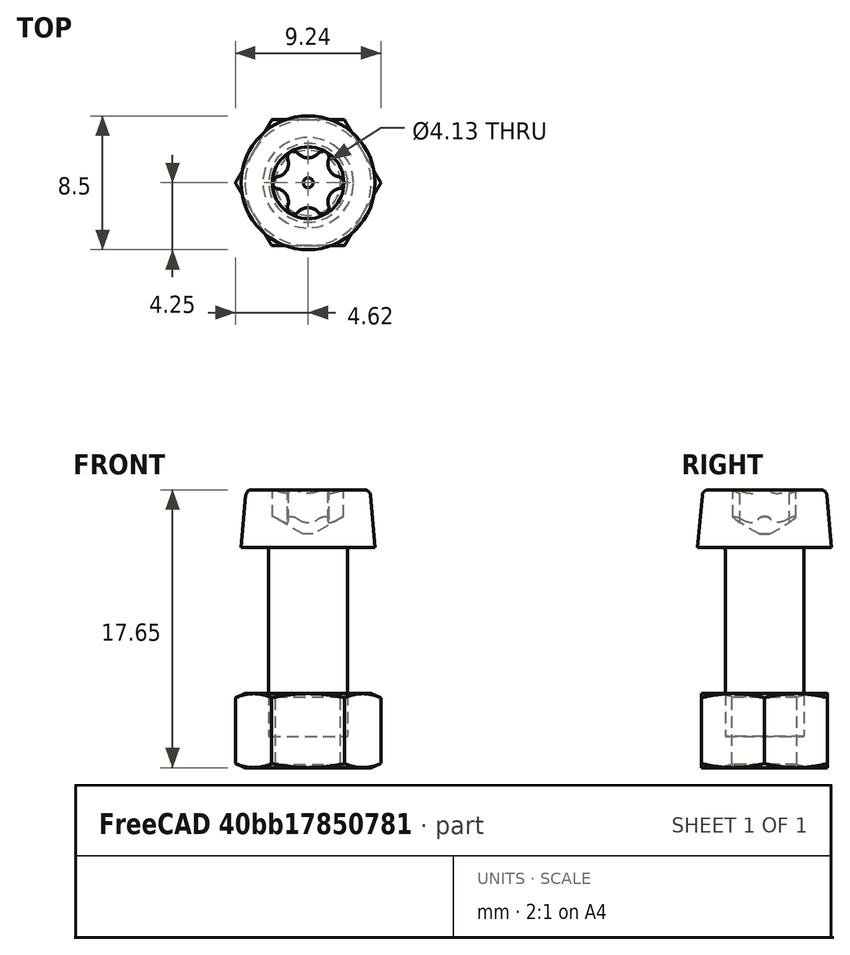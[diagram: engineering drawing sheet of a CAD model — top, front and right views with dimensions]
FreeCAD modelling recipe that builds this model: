
FCSTD DOCUMENT  (FreeCAD 0.20R29177 +426 (Git))
Label: assembly
License: All rights reserved
LicenseURL: http://en.wikipedia.org/wiki/All_rights_reserved
objects: App::DocumentObjectGroup×3, App::Link×3, Part::FeaturePython×2, PartDesign::CoordinateSystem×1, App::FeaturePython×1, App::Part×1
note: 3 computed .brp shape members not serialized (recipe doc carries the construction recipe); baked Part::Feature solids carry a one-line shape summary decoded from their .brp
EXTERNAL_REF file=clamp.FCStd obj=LCS_1
EXTERNAL_REF file=clamp.FCStd obj=Body
EXTERNAL_REF file=clamp.FCStd obj=CircleAxis_1
EXTERNAL_REF file=rectangle.FCStd obj=CircleAxis_1
EXTERNAL_REF file=rectangle.FCStd obj=Part

FEATURE [App::DocumentObjectGroup] Parts
FEATURE [PartDesign::CoordinateSystem] LCS_Origin
  AttacherType = Attacher::AttachEngine3D
  MapMode = 2
  Support = -> [X_Axis]
FEATURE [App::DocumentObjectGroup] Constraints
FEATURE [App::FeaturePython] Variables  # WARN: FeaturePython — macro-defined, semantics opaque (R4)
  Type = App::PropertyContainer
FEATURE [App::DocumentObjectGroup] Configurations
FEATURE [App::Link] clamp
  AttachedBy = #LCS_1
  AttachedTo = Parent Assembly#LCS_Origin
  LinkedObject = -> <external clamp.FCStd>#Body
  SolverId = Asm4EE
  expr: Placement = LCS_Origin.Placement * AttachmentOffset * clamp#LCS_1.Placement ^ -1
FEATURE [Part::FeaturePython] Screw  label="M5x12-Screw"  # WARN: FeaturePython — macro-defined, semantics opaque (R4)
  AttachedBy = Origin
  AttachedTo = clamp#CircleAxis_1
  Diameter = 7
  Invert = false
  LeftHanded = false
  Length = 3
  LengthCustom = 12
  MatchOuter = false
  OffsetAngle = 0
  Placement = pos=(-25,-5,3) rot=(0,0,1;3.14159rad)
  SolverId = Asm4EE
  Thread = false
  Type = 54
  expr: Placement = clamp.Placement * clamp#CircleAxis_1.Placement * AttachmentOffset
FEATURE [App::Link] RectanglePart
  AttachedBy = #CircleAxis_1
  AttachedTo = clamp#CircleAxis_1
  AttachmentOffset = pos=(0,0,-3) rot=(0,0,1;4.71239rad)
  LinkPlacement = pos=(-25,30,-3) rot=(0,0,-1;4.71239rad)
  LinkedObject = -> <external rectangle.FCStd>#Part
  Placement = pos=(-25,30,-3) rot=(0,0,-1;4.71239rad)
  SolverId = Asm4EE
  expr: Placement = clamp.Placement * clamp#CircleAxis_1.Placement * AttachmentOffset * rectangle#CircleAxis_1.Placement ^ -1
FEATURE [Part::FeaturePython] Nut  label="M5-Nut"  # WARN: FeaturePython — macro-defined, semantics opaque (R4)
  AttachedBy = Origin
  AttachedTo = clamp#CircleAxis_1
  AttachmentOffset = pos=(0,0,-14) rot=(0,0,1;0rad)
  Diameter = 7
  Invert = false
  LeftHanded = false
  MatchOuter = false
  OffsetAngle = 0
  Placement = pos=(-25,-5,-11) rot=(0,0,1;3.14159rad)
  SolverId = Asm4EE
  Thread = false
  Type = 31
  expr: Placement = clamp.Placement * clamp#CircleAxis_1.Placement * AttachmentOffset
FEATURE [App::Link] Body
  AttachedBy = #CircleAxis_1
  AttachedTo = clamp#CircleAxis_1
  AttachmentOffset = pos=(0,0,-9) rot=(1,0,0;3.14159rad)
  LinkPlacement = pos=(0,-10,-3) rot=(-1,0,0;3.14159rad)
  LinkedObject = -> <external clamp.FCStd>#Body
  Placement = pos=(0,-10,-3) rot=(-1,0,0;3.14159rad)
  SolverId = Asm4EE
  expr: Placement = clamp.Placement * clamp#CircleAxis_1.Placement * AttachmentOffset * clamp#CircleAxis_1.Placement ^ -1
FEATURE [App::Part] Assembly
  AssemblyType = Part::Link
  Group = -> [LCS_Origin,Constraints,Variables,Configurations,clamp,Screw,RectanglePart,Nut,Body]
  Origin = -> Origin
  Type = Assembly

RESOLVED EXTERNAL PARTS (link-assembly join: the EXTERNAL_REF files above that resolve inside this repo's crawl, each included once):
---- part clamp.FCStd = doc fcstd_29977836d994 ----
FCSTD DOCUMENT  (FreeCAD 0.20R29177 +426 (Git))
Label: clamp
License: All rights reserved
LicenseURL: http://en.wikipedia.org/wiki/All_rights_reserved
objects: Sketcher::SketchObject×2, PartDesign::Pad×1, PartDesign::Pocket×1, PartDesign::CoordinateSystem×1, PartDesign::Line×1, PartDesign::Body×1
note: 9 computed .brp shape members not serialized (recipe doc carries the construction recipe); baked Part::Feature solids carry a one-line shape summary decoded from their .brp

FEATURE [Sketcher::SketchObject] Sketch
  FullyConstrained = true
  MapMode = 5
  Placement = pos=(0,0,0) rot=(1,0,0;1.5708rad)
  Support = -> [XZ_Plane]
  sketch-geometry (10):
    g0: LineSegment StartX=-30 StartY=0 StartZ=0 EndX=-17 EndY=0 EndZ=0
    g1: LineSegment StartX=-30 StartY=0 StartZ=0 EndX=-30 EndY=3 EndZ=0
    g2: LineSegment StartX=30 StartY=3 StartZ=0 EndX=30 EndY=0 EndZ=0
    g3: ArcOfCircle CenterX=0 CenterY=0 CenterZ=0 NormalX=0 NormalY=0 NormalZ=1 AngleXU=0 Radius=20.2237 StartAngle=0.14889 EndAngle=2.9927
    g4: LineSegment StartX=-30 StartY=3 StartZ=0 EndX=-20 EndY=3 EndZ=0
    g5: LineSegment StartX=20 StartY=3 StartZ=0 EndX=30 EndY=3 EndZ=0
    g6: ArcOfCircle CenterX=0 CenterY=0 CenterZ=0 NormalX=0 NormalY=0 NormalZ=1 AngleXU=0 Radius=17.2627 StartAngle=0.174672 EndAngle=2.96692
    g7: LineSegment StartX=17 StartY=3 StartZ=0 EndX=17 EndY=-3.83895e-05 EndZ=0
    g8: LineSegment StartX=-17 StartY=3 StartZ=0 EndX=-17 EndY=0 EndZ=0
    g9: LineSegment StartX=17 StartY=-3.83895e-05 StartZ=0 EndX=30 EndY=0 EndZ=0
  constraints (30):
    c: PointOnObject(g0,g-1)
    c: PointOnObject(g9,g-1)
    c: Coincident(g0,g1)
    c: Vertical(g1)
    c: Coincident(g2,g9)
    c: Coincident(g1,g4)
    c: Coincident(g4,g3)
    c: Coincident(g5,g3)
    c: Coincident(g5,g2)
    c: Horizontal(g5)
    c: Horizontal(g4)
    c: Equal(g2,g1)
    c: Vertical(g2)
    c: Equal(g5,g4)
    c: DistanceX(g5,g5) = 10
    c: DistanceX(g0,g9) = 60
    c: DistanceY(g2,g2) = 3
    c: Coincident(g3,g-1)
    c: Horizontal(g6,g3)
    c: Horizontal(g6,g3)
    c: Coincident(g7,g6)
    c: Vertical(g7)
    c: Coincident(g8,g6)
    c: Vertical(g8)
    c: Coincident(g6,g3)
    c: Coincident(g0,g8)
    c: Coincident(g9,g7)
    c: DistanceX(g6,g3) = 3
    c: Equal(g0,g9)
    c: PointOnObject(g0,g-1)
FEATURE [PartDesign::Pad] Pad
  Direction = (0,-1,-2e-16)
  Length = 10
  Length2 = 10
  Placement = pos=(0,0,0) rot=(1,0,0;1.5708rad)
  Profile = -> Sketch
  ReferenceAxis = -> Sketch [N_Axis]
  Type = 0
FEATURE [Sketcher::SketchObject] Sketch001
  ExternalGeometry = -> [Pad]
  FullyConstrained = true
  MapMode = 5
  Placement = pos=(0,7e-16,3) rot=(0,0,1;3.14159rad)
  Support = -> [Pad]
  sketch-geometry (2):
    g0: Circle CenterX=-25 CenterY=5 CenterZ=0 NormalX=0 NormalY=0 NormalZ=1 AngleXU=0 Radius=2.5
    g1: Circle CenterX=25 CenterY=5 CenterZ=0 NormalX=0 NormalY=0 NormalZ=1 AngleXU=0 Radius=2.5
  constraints (4):
    c: Symmetric(g-6,g-7,g1)
    c: Symmetric(g-3,g-4,g0)
    c: Equal(g1,g0)
    c: Diameter(g1) = 5
FEATURE [PartDesign::Pocket] Pocket
  BaseFeature = -> Pad
  Direction = (0,-2e-16,-1)
  Length = 4
  Length2 = 5
  Placement = pos=(0,0,0) rot=(1,0,0;1.5708rad)
  Profile = -> Sketch001
  ReferenceAxis = -> Sketch001 [N_Axis]
  Type = 0
FEATURE [PartDesign::CoordinateSystem] LCS_1
  AttacherType = Attacher::AttachEngine3D
  Support = -> [Pocket]
FEATURE [PartDesign::Line] CircleAxis_1
  AttacherType = Attacher::AttachEngineLine
  Length = 14.0907
  MapMode = 19
  Placement = pos=(-25,-5,3) rot=(0,0,1;3.14159rad)
  ResizeMode = 1
  Support = -> [Pocket]
FEATURE [PartDesign::Body] Body
  Group = -> [Sketch,Pad,Sketch001,Pocket,LCS_1,CircleAxis_1]
  Origin = -> Origin
  Tip = -> Pocket
---- part rectangle.FCStd = doc fcstd_6d6c4f5b0d0f ----
FCSTD DOCUMENT  (FreeCAD 0.20R29177 +426 (Git))
Label: rectangle
License: All rights reserved
LicenseURL: http://en.wikipedia.org/wiki/All_rights_reserved
objects: Sketcher::SketchObject×1, Part::Extrusion×1, PartDesign::Line×1, App::Part×1
note: 3 computed .brp shape members not serialized (recipe doc carries the construction recipe); baked Part::Feature solids carry a one-line shape summary decoded from their .brp

FEATURE [Sketcher::SketchObject] Sketch
  FullyConstrained = true
  sketch-geometry (6):
    g0: LineSegment StartX=40 StartY=-6 StartZ=0 EndX=40 EndY=6 EndZ=0
    g1: LineSegment StartX=40 StartY=6 StartZ=0 EndX=-40 EndY=6 EndZ=0
    g2: LineSegment StartX=-40 StartY=6 StartZ=0 EndX=-40 EndY=-6 EndZ=0
    g3: LineSegment StartX=-40 StartY=-6 StartZ=0 EndX=40 EndY=-6 EndZ=0
    g4: GeomPoint X=0 Y=0 Z=0
    g5: Circle CenterX=-35 CenterY=0 CenterZ=0 NormalX=0 NormalY=0 NormalZ=1 AngleXU=0 Radius=2.5
  constraints (15):
    c: Coincident(g0,g1)
    c: Coincident(g1,g2)
    c: Coincident(g2,g3)
    c: Coincident(g3,g0)
    c: Horizontal(g1)
    c: Horizontal(g3)
    c: Vertical(g0)
    c: Vertical(g2)
    c: Symmetric(g1,g0,g4)
    c: Coincident(g4,g-1)
    c: DistanceX(g1,g1) = 80
    c: DistanceY(g2,g2) = 12
    c: DistanceX(g1,g5) = 5
    c: PointOnObject(g5,g-1)
    c: Diameter(g5) = 5
FEATURE [Part::Extrusion] Extrude
  Base = -> Sketch
  Dir = (0,0,1)
  DirMode = 2
  FaceMakerClass = Part::FaceMakerBullseye
  LengthFwd = 3
  LengthRev = 0
  Solid = true
  Symmetric = false
FEATURE [PartDesign::Line] CircleAxis_1
  AttacherType = Attacher::AttachEngineLine
  Length = 14.0907
  MapMode = 19
  Placement = pos=(-35,0,3) rot=(0,0,1;0rad)
  ResizeMode = 1
  Support = -> [Extrude]
FEATURE [App::Part] Part  label="RectanglePart"
  Group = -> [Sketch,Extrude,CircleAxis_1]
  Origin = -> Origin
